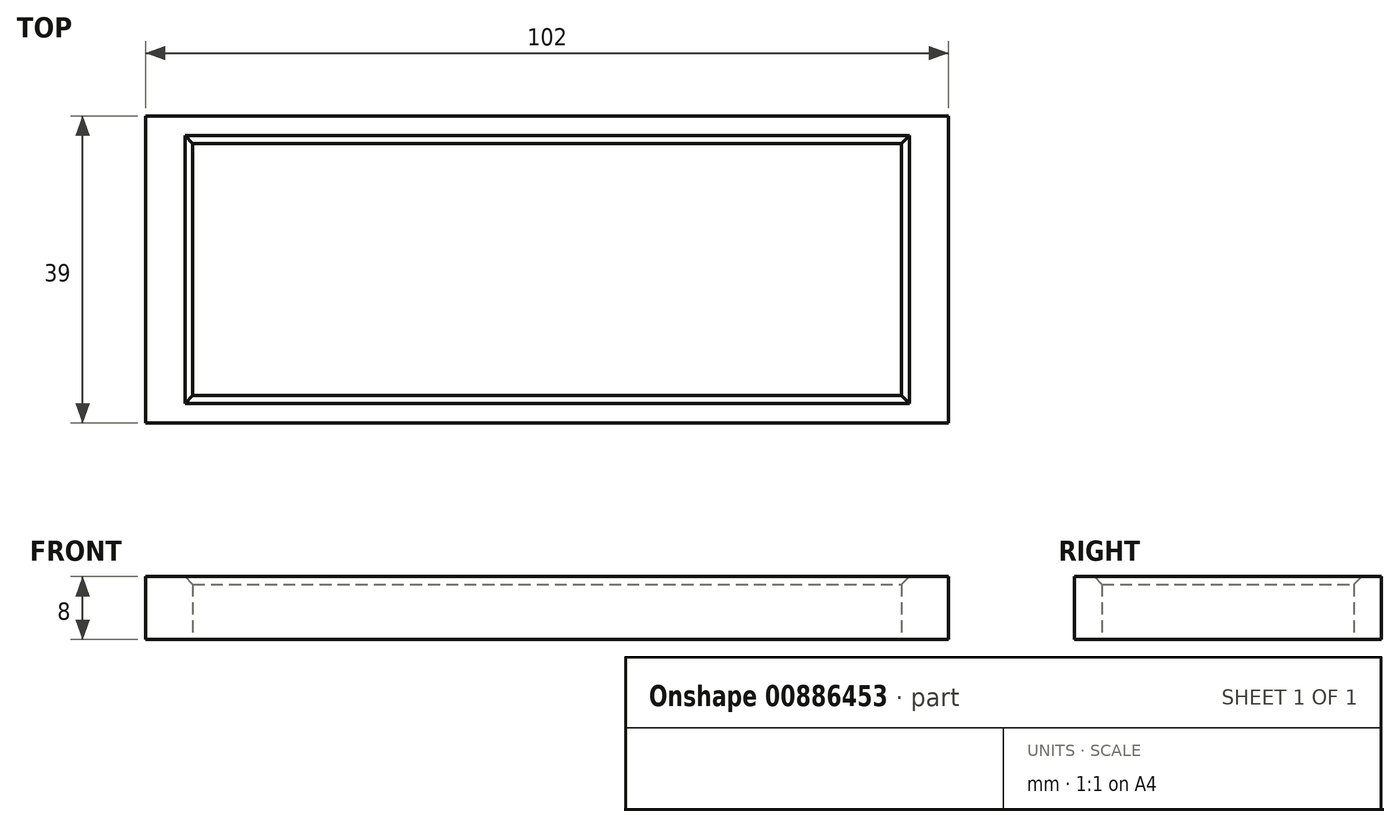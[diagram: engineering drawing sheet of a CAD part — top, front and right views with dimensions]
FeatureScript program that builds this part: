
annotation { "Feature Type Name" : "Feature", "Feature Type Description" : "" }
export const myFeature = defineFeature(function(context is Context, id is Id, definition is map)
    precondition{}
    {
        {
            var Q0;
            Q0=qCreatedBy(makeId("Top.planeOp"),FACE);
            var sketch = newSketch(context, id + "F0", { "sketchPlane" : qUnion([Q0])});
            skLineSegment(sketch, "E0.bottom", {"start": v(51, -19.5) * mm, "end": v(-51, -19.5) * mm});
            skLineSegment(sketch, "E0.top", {"start": v(51, 19.5) * mm, "end": v(-51, 19.5) * mm});
            skLineSegment(sketch, "E0.left", {"start": v(51, -19.5) * mm, "end": v(51, 19.5) * mm});
            skLineSegment(sketch, "E0.right", {"start": v(-51, -19.5) * mm, "end": v(-51, 19.5) * mm});
            skPoint(sketch, "E0.middle", {"position": v(0, 0) * mm});
            skLineSegment(sketch, "E1.bottom", {"start": v(45, -16) * mm, "end": v(-45, -16) * mm});
            skLineSegment(sketch, "E1.top", {"start": v(45, 16) * mm, "end": v(-45, 16) * mm});
            skLineSegment(sketch, "E1.left", {"start": v(45, -16) * mm, "end": v(45, 16) * mm});
            skLineSegment(sketch, "E1.right", {"start": v(-45, -16) * mm, "end": v(-45, 16) * mm});
            skSolve(sketch);
        }
        {
            var Q0;
            Q0 = qSketchRegion(id + "F0", true);
            extrude(context, id + "F1", {"entities" : qUnion([Q0]), "depth" : 8 * mm, "offsetDistance" : 25 * mm});
        }
        {
            var Q0;
            Q0=makeQuery(id+"F1.opExtrude","CAP_EDGE",EDGE,{"disambiguationData":[OSD([sQuery(id+"F0.wireOp",EDGE,"E1.top")])],"isStart":false});
            var Q1;
            Q1=makeQuery(id+"F1.opExtrude","CAP_EDGE",EDGE,{"disambiguationData":[OSD([sQuery(id+"F0.wireOp",EDGE,"E1.left")])],"isStart":false});
            var Q2;
            Q2=makeQuery(id+"F1.opExtrude","CAP_EDGE",EDGE,{"disambiguationData":[OSD([sQuery(id+"F0.wireOp",EDGE,"E1.bottom")])],"isStart":false});
            var Q3;
            Q3=makeQuery(id+"F1.opExtrude","CAP_EDGE",EDGE,{"disambiguationData":[OSD([sQuery(id+"F0.wireOp",EDGE,"E1.right")])],"isStart":false});
            chamfer(context, id + "F2", {"entities" : qUnion([Q0, Q1, Q2, Q3]), "width" : 1 * mm, "tangentPropagation" : true});
        }
    });
